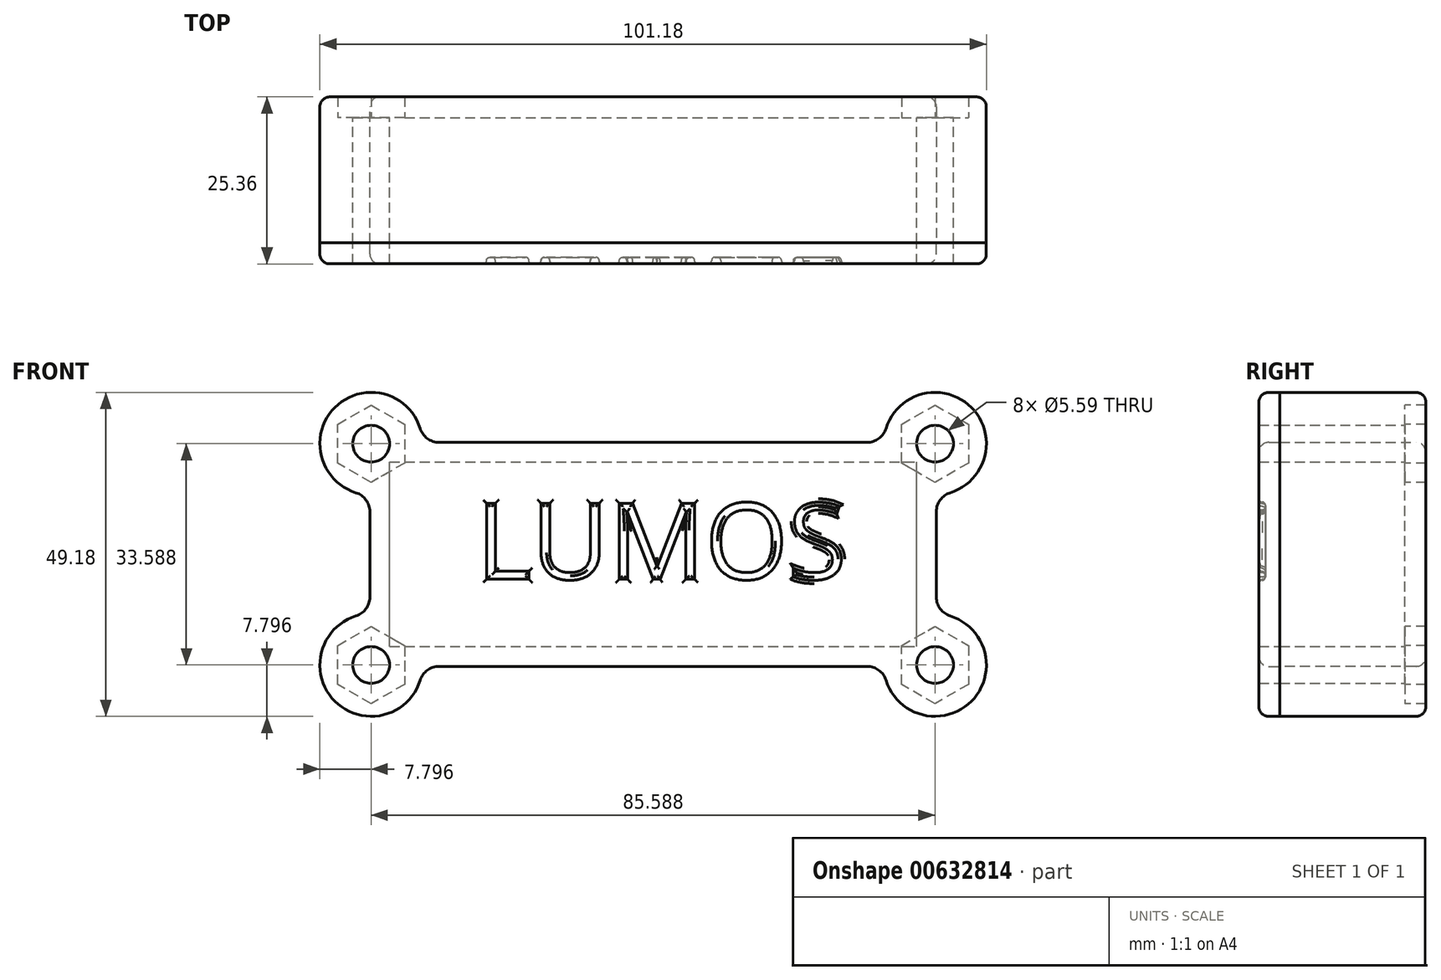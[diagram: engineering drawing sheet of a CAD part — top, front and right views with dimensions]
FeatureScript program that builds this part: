
annotation { "Feature Type Name" : "Feature", "Feature Type Description" : "" }
export const myFeature = defineFeature(function(context is Context, id is Id, definition is map)
    precondition{}
    {
        {
            var Q0;
            Q0=qCreatedBy(makeId("Front.planeOp"),FACE);
            var sketch = newSketch(context, id + "F0", { "sketchPlane" : qUnion([Q0])});
            skLineSegment(sketch, "E0.bottom", {"start": v(0, 0) * mm, "end": v(80, 0) * mm});
            skLineSegment(sketch, "E0.top", {"start": v(0, 28) * mm, "end": v(80, 28) * mm});
            skLineSegment(sketch, "E0.left", {"start": v(0, 0) * mm, "end": v(0, 28) * mm});
            skLineSegment(sketch, "E0.right", {"start": v(80, 0) * mm, "end": v(80, 28) * mm});
            skCircle(sketch, "E1", {"center": v(82.8, 30.8) * mm, "radius": 2.8 * mm});
            skCircle(sketch, "E2", {"center": v(82.8, -2.8) * mm, "radius": 2.8 * mm});
            skCircle(sketch, "E3", {"center": v(-2.8, -2.8) * mm, "radius": 2.8 * mm});
            skCircle(sketch, "E4", {"center": v(-2.8, 30.8) * mm, "radius": 2.8 * mm});
            skArc(sketch, "E5", {"start": v(5, 31) * mm, "mid": v(-8.3, 36.3) * mm, "end": v(-3, 23) * mm});
            skArc(sketch, "E6", {"start": v(83, 23) * mm, "mid": v(88.3, 36.3) * mm, "end": v(75, 31) * mm});
            skArc(sketch, "E7", {"start": v(75, -3) * mm, "mid": v(88.3, -8.3) * mm, "end": v(83, 5) * mm});
            skLineSegment(sketch, "E8.0", {"start": v(5, 31) * mm, "end": v(75, 31) * mm});
            skLineSegment(sketch, "E8.1", {"start": v(-3, 5) * mm, "end": v(-3, 23) * mm});
            skLineSegment(sketch, "E8.2", {"start": v(5, -3) * mm, "end": v(75, -3) * mm});
            skLineSegment(sketch, "E8.3", {"start": v(83, 5) * mm, "end": v(83, 23) * mm});
            skArc(sketch, "E9.trimOffspring", {"start": v(-3, 5) * mm, "mid": v(-8.3, -8.3) * mm, "end": v(5, -3) * mm});
            skSolve(sketch);
        }
        {
            var Q0;
            Q0=makeQuery(id+"F0.imprint","IMPRINT",FACE,{"disambiguationData":[TD([[makeQuery(id+"F0.imprint","IMPRINT",EDGE,{"derivedFrom":sQuery(id+"F0.wireOp",EDGE,"E0.bottom")}),-1.0]])]});
            extrude(context, id + "F1", {"entities" : qUnion([Q0]), "depth" : 19 * mm, "offsetDistance" : 25 * mm});
        }
        {
            var Q0;
            Q0=qCreatedBy(makeId("Front.planeOp"),FACE);
            var sketch = newSketch(context, id + "F2", { "sketchPlane" : qUnion([Q0])});
            skLineSegment(sketch, "E10.0", {"start": v(5, -3) * mm, "end": v(75, -3) * mm});
            skArc(sketch, "E11.0", {"start": v(-3, 5) * mm, "mid": v(-8.3, -8.3) * mm, "end": v(5, -3) * mm});
            skArc(sketch, "E12.0", {"start": v(75, -3) * mm, "mid": v(88.3, -8.3) * mm, "end": v(83, 5) * mm});
            skLineSegment(sketch, "E13.0", {"start": v(83, 5) * mm, "end": v(83, 23) * mm});
            skArc(sketch, "E14.0", {"start": v(83, 23) * mm, "mid": v(88.3, 36.3) * mm, "end": v(75, 31) * mm});
            skLineSegment(sketch, "E15.0", {"start": v(5, 31) * mm, "end": v(75, 31) * mm});
            skArc(sketch, "E16.0", {"start": v(5, 31) * mm, "mid": v(-8.3, 36.3) * mm, "end": v(-3, 23) * mm});
            skLineSegment(sketch, "E17.0", {"start": v(-3, 5) * mm, "end": v(-3, 23) * mm});
            skCircle(sketch, "E18.0", {"center": v(-2.8, -2.8) * mm, "radius": 2.8 * mm});
            skCircle(sketch, "E19.0", {"center": v(-2.8, 30.8) * mm, "radius": 2.8 * mm});
            skCircle(sketch, "E20.0", {"center": v(82.8, -2.8) * mm, "radius": 2.8 * mm});
            skCircle(sketch, "E21.0", {"center": v(82.8, 30.8) * mm, "radius": 2.8 * mm});
            skSolve(sketch);
        }
        {
            var Q0;
            Q0 = qSketchRegion(id + "F2", true);
            extrude(context, id + "F3", {"entities" : qUnion([Q0]), "operationType" : NewBodyOperationType.ADD, "oppositeDirection" : true, "depth" : 3.17 * mm, "offsetDistance" : 25 * mm});
        }
        {
            var Q0;
            Q0=makeQuery(id+"F3.boolean.opBoolean","MERGE",EDGE,{"derivedFrom":[makeQuery(id+"F1.opExtrude","SWEPT_EDGE",EDGE,{"disambiguationData":[OSD([sQuery(id+"F0.wireOp",EDGE,"E8.2"),sQuery(id+"F0.wireOp",EDGE,"E9.trimOffspring")])]}),makeQuery(id+"F3.opExtrude","SWEPT_EDGE",EDGE,{"disambiguationData":[OSD([sQuery(id+"F2.wireOp",EDGE,"E10.0"),sQuery(id+"F2.wireOp",EDGE,"E11.0")])]})]});
            var Q1;
            Q1=makeQuery(id+"F3.boolean.opBoolean","MERGE",EDGE,{"derivedFrom":[makeQuery(id+"F1.opExtrude","SWEPT_EDGE",EDGE,{"disambiguationData":[OSD([sQuery(id+"F0.wireOp",EDGE,"E6"),sQuery(id+"F0.wireOp",EDGE,"E8.3")])]}),makeQuery(id+"F3.opExtrude","SWEPT_EDGE",EDGE,{"disambiguationData":[OSD([sQuery(id+"F2.wireOp",EDGE,"E13.0"),sQuery(id+"F2.wireOp",EDGE,"E14.0")])]})]});
            var Q2;
            Q2=makeQuery(id+"F3.boolean.opBoolean","MERGE",EDGE,{"derivedFrom":[makeQuery(id+"F1.opExtrude","SWEPT_EDGE",EDGE,{"disambiguationData":[OSD([sQuery(id+"F0.wireOp",EDGE,"E7"),sQuery(id+"F0.wireOp",EDGE,"E8.2")])]}),makeQuery(id+"F3.opExtrude","SWEPT_EDGE",EDGE,{"disambiguationData":[OSD([sQuery(id+"F2.wireOp",EDGE,"E10.0"),sQuery(id+"F2.wireOp",EDGE,"E12.0")])]})]});
            var Q3;
            Q3=makeQuery(id+"F3.boolean.opBoolean","MERGE",EDGE,{"derivedFrom":[makeQuery(id+"F1.opExtrude","SWEPT_EDGE",EDGE,{"disambiguationData":[OSD([sQuery(id+"F0.wireOp",EDGE,"E7"),sQuery(id+"F0.wireOp",EDGE,"E8.3")])]}),makeQuery(id+"F3.opExtrude","SWEPT_EDGE",EDGE,{"disambiguationData":[OSD([sQuery(id+"F2.wireOp",EDGE,"E12.0"),sQuery(id+"F2.wireOp",EDGE,"E13.0")])]})]});
            var Q4;
            Q4=makeQuery(id+"F3.boolean.opBoolean","MERGE",EDGE,{"derivedFrom":[makeQuery(id+"F1.opExtrude","SWEPT_EDGE",EDGE,{"disambiguationData":[OSD([sQuery(id+"F0.wireOp",EDGE,"E6"),sQuery(id+"F0.wireOp",EDGE,"E8.0")])]}),makeQuery(id+"F3.opExtrude","SWEPT_EDGE",EDGE,{"disambiguationData":[OSD([sQuery(id+"F2.wireOp",EDGE,"E14.0"),sQuery(id+"F2.wireOp",EDGE,"E15.0")])]})]});
            var Q5;
            Q5=makeQuery(id+"F3.boolean.opBoolean","MERGE",EDGE,{"derivedFrom":[makeQuery(id+"F1.opExtrude","SWEPT_EDGE",EDGE,{"disambiguationData":[OSD([sQuery(id+"F0.wireOp",EDGE,"E8.1"),sQuery(id+"F0.wireOp",EDGE,"E9.trimOffspring")])]}),makeQuery(id+"F3.opExtrude","SWEPT_EDGE",EDGE,{"disambiguationData":[OSD([sQuery(id+"F2.wireOp",EDGE,"E11.0"),sQuery(id+"F2.wireOp",EDGE,"E17.0")])]})]});
            var Q6;
            Q6=makeQuery(id+"F3.boolean.opBoolean","MERGE",EDGE,{"derivedFrom":[makeQuery(id+"F1.opExtrude","SWEPT_EDGE",EDGE,{"disambiguationData":[OSD([sQuery(id+"F0.wireOp",EDGE,"E5"),sQuery(id+"F0.wireOp",EDGE,"E8.1")])]}),makeQuery(id+"F3.opExtrude","SWEPT_EDGE",EDGE,{"disambiguationData":[OSD([sQuery(id+"F2.wireOp",EDGE,"E16.0"),sQuery(id+"F2.wireOp",EDGE,"E17.0")])]})]});
            var Q7;
            Q7=makeQuery(id+"F3.boolean.opBoolean","MERGE",EDGE,{"derivedFrom":[makeQuery(id+"F1.opExtrude","SWEPT_EDGE",EDGE,{"disambiguationData":[OSD([sQuery(id+"F0.wireOp",EDGE,"E5"),sQuery(id+"F0.wireOp",EDGE,"E8.0")])]}),makeQuery(id+"F3.opExtrude","SWEPT_EDGE",EDGE,{"disambiguationData":[OSD([sQuery(id+"F2.wireOp",EDGE,"E15.0"),sQuery(id+"F2.wireOp",EDGE,"E16.0")])]})]});
            fillet(context, id + "F4", {"entities" : qUnion([Q0, Q1, Q2, Q3, Q4, Q5, Q6, Q7]), "radius" : 3 * mm, "tangentPropagation" : true, "allowEdgeOverflow" : false});
        }
        {
            var Q0;
            Q0=makeQuery(id+"F3.opExtrude","CAP_EDGE",EDGE,{"disambiguationData":[OSD([sQuery(id+"F2.wireOp",EDGE,"E15.0")])],"isStart":false});
            fillet(context, id + "F5", {"entities" : qUnion([Q0]), "radius" : 1.5 * mm, "tangentPropagation" : true, "allowEdgeOverflow" : false});
        }
        {
            var Q0;
            Q0=qCreatedBy(makeId("Front.planeOp"),FACE);
            var sketch = newSketch(context, id + "F6", { "sketchPlane" : qUnion([Q0])});
            skCircle(sketch, "E22.cCircle", {"center": v(-2.8, -2.8) * mm, "radius": 5.08 * mm, "construction": true});
            skLineSegment(sketch, "E22.0", {"start": v(2.29, 0.14) * mm, "end": v(2.29, -5.73) * mm});
            skLineSegment(sketch, "E22.1", {"start": v(2.29, -5.73) * mm, "end": v(-2.8, -8.66) * mm});
            skLineSegment(sketch, "E22.2", {"start": v(-2.8, -8.66) * mm, "end": v(-7.87, -5.73) * mm});
            skLineSegment(sketch, "E22.3", {"start": v(-7.87, -5.73) * mm, "end": v(-7.87, 0.14) * mm});
            skLineSegment(sketch, "E22.4", {"start": v(-7.87, 0.14) * mm, "end": v(-2.8, 3.07) * mm});
            skLineSegment(sketch, "E22.5", {"start": v(-2.8, 3.07) * mm, "end": v(2.29, 0.14) * mm});
            skPoint(sketch, "E22.0.midPoint", {"position": v(2.29, -2.8) * mm});
            skCircle(sketch, "E23.cCircle", {"center": v(-2.8, 30.8) * mm, "radius": 5.08 * mm, "construction": true});
            skLineSegment(sketch, "E23.0", {"start": v(2.29, 33.73) * mm, "end": v(2.29, 27.86) * mm});
            skLineSegment(sketch, "E23.1", {"start": v(2.29, 27.86) * mm, "end": v(-2.8, 24.93) * mm});
            skLineSegment(sketch, "E23.2", {"start": v(-2.8, 24.93) * mm, "end": v(-7.87, 27.86) * mm});
            skLineSegment(sketch, "E23.3", {"start": v(-7.87, 27.86) * mm, "end": v(-7.87, 33.73) * mm});
            skLineSegment(sketch, "E23.4", {"start": v(-7.87, 33.73) * mm, "end": v(-2.8, 36.66) * mm});
            skLineSegment(sketch, "E23.5", {"start": v(-2.8, 36.66) * mm, "end": v(2.29, 33.73) * mm});
            skPoint(sketch, "E23.0.midPoint", {"position": v(2.29, 30.8) * mm});
            skCircle(sketch, "E24.cCircle", {"center": v(82.8, 30.8) * mm, "radius": 5.08 * mm, "construction": true});
            skLineSegment(sketch, "E24.0", {"start": v(87.87, 33.73) * mm, "end": v(87.87, 27.86) * mm});
            skLineSegment(sketch, "E24.1", {"start": v(87.87, 27.86) * mm, "end": v(82.8, 24.93) * mm});
            skLineSegment(sketch, "E24.2", {"start": v(82.8, 24.93) * mm, "end": v(77.71, 27.86) * mm});
            skLineSegment(sketch, "E24.3", {"start": v(77.71, 27.86) * mm, "end": v(77.71, 33.73) * mm});
            skLineSegment(sketch, "E24.4", {"start": v(77.71, 33.73) * mm, "end": v(82.8, 36.66) * mm});
            skLineSegment(sketch, "E24.5", {"start": v(82.8, 36.66) * mm, "end": v(87.87, 33.73) * mm});
            skPoint(sketch, "E24.0.midPoint", {"position": v(87.87, 30.8) * mm});
            skCircle(sketch, "E25.cCircle", {"center": v(82.8, -2.8) * mm, "radius": 5.08 * mm, "construction": true});
            skLineSegment(sketch, "E25.0", {"start": v(77.71, -5.73) * mm, "end": v(77.71, 0.14) * mm});
            skLineSegment(sketch, "E25.1", {"start": v(77.71, 0.14) * mm, "end": v(82.8, 3.07) * mm});
            skLineSegment(sketch, "E25.2", {"start": v(82.8, 3.07) * mm, "end": v(87.87, 0.14) * mm});
            skLineSegment(sketch, "E25.3", {"start": v(87.87, 0.14) * mm, "end": v(87.87, -5.73) * mm});
            skLineSegment(sketch, "E25.4", {"start": v(87.87, -5.73) * mm, "end": v(82.8, -8.66) * mm});
            skLineSegment(sketch, "E25.5", {"start": v(82.8, -8.66) * mm, "end": v(77.71, -5.73) * mm});
            skPoint(sketch, "E25.0.midPoint", {"position": v(77.71, -2.8) * mm});
            skSolve(sketch);
        }
        {
            var Q0;
            Q0 = qSketchRegion(id + "F6", true);
            extrude(context, id + "F7", {"entities" : qUnion([Q0]), "operationType" : NewBodyOperationType.REMOVE, "oppositeDirection" : true, "depth" : 25 * mm, "offsetDistance" : 25 * mm});
        }
        {
            var Q0;
            Q0=makeQuery(id+"F1.opExtrude","CAP_FACE",FACE,{"disambiguationData":[OSD([sQuery(id+"F0.wireOp",EDGE,"E0.bottom"),sQuery(id+"F0.wireOp",EDGE,"E0.top"),sQuery(id+"F0.wireOp",EDGE,"E0.left"),sQuery(id+"F0.wireOp",EDGE,"E0.right"),sQuery(id+"F0.wireOp",EDGE,"E1"),sQuery(id+"F0.wireOp",EDGE,"E2"),sQuery(id+"F0.wireOp",EDGE,"E3"),sQuery(id+"F0.wireOp",EDGE,"E4"),sQuery(id+"F0.wireOp",EDGE,"E5"),sQuery(id+"F0.wireOp",EDGE,"E6"),sQuery(id+"F0.wireOp",EDGE,"E7"),sQuery(id+"F0.wireOp",EDGE,"E8.0"),sQuery(id+"F0.wireOp",EDGE,"E8.1"),sQuery(id+"F0.wireOp",EDGE,"E8.2"),sQuery(id+"F0.wireOp",EDGE,"E8.3"),sQuery(id+"F0.wireOp",EDGE,"E9.trimOffspring")])],"isStart":false});
            var sketch = newSketch(context, id + "F8", { "sketchPlane" : qUnion([Q0])});
            skArc(sketch, "E26.0", {"start": v(4.65, 33.1) * mm, "mid": v(-8.3, 36.3) * mm, "end": v(-5.1, 23.35) * mm});
            skArc(sketch, "E26.1", {"start": v(7.51, 31) * mm, "mid": v(5.73, 31.58) * mm, "end": v(4.65, 33.1) * mm});
            skLineSegment(sketch, "E26.2", {"start": v(7.51, 31) * mm, "end": v(72.49, 31) * mm});
            skArc(sketch, "E26.3", {"start": v(75.35, 33.1) * mm, "mid": v(74.27, 31.58) * mm, "end": v(72.49, 31) * mm});
            skArc(sketch, "E26.4", {"start": v(85.1, 23.35) * mm, "mid": v(88.3, 36.3) * mm, "end": v(75.35, 33.1) * mm});
            skLineSegment(sketch, "E26.5", {"start": v(83, 7.51) * mm, "end": v(83, 20.49) * mm});
            skArc(sketch, "E26.6", {"start": v(83, 20.49) * mm, "mid": v(83.58, 22.27) * mm, "end": v(85.1, 23.35) * mm});
            skArc(sketch, "E26.7", {"start": v(85.1, 4.65) * mm, "mid": v(83.58, 5.73) * mm, "end": v(83, 7.51) * mm});
            skArc(sketch, "E26.8", {"start": v(75.35, -5.1) * mm, "mid": v(88.3, -8.3) * mm, "end": v(85.1, 4.65) * mm});
            skLineSegment(sketch, "E26.9", {"start": v(7.51, -3) * mm, "end": v(72.49, -3) * mm});
            skArc(sketch, "E26.10", {"start": v(72.49, -3) * mm, "mid": v(74.27, -3.58) * mm, "end": v(75.35, -5.1) * mm});
            skArc(sketch, "E26.11", {"start": v(4.65, -5.1) * mm, "mid": v(5.73, -3.58) * mm, "end": v(7.51, -3) * mm});
            skArc(sketch, "E26.12", {"start": v(-5.1, 4.65) * mm, "mid": v(-8.3, -8.3) * mm, "end": v(4.65, -5.1) * mm});
            skArc(sketch, "E26.13", {"start": v(-3, 7.51) * mm, "mid": v(-3.58, 5.73) * mm, "end": v(-5.1, 4.65) * mm});
            skLineSegment(sketch, "E26.14", {"start": v(-3, 7.51) * mm, "end": v(-3, 20.49) * mm});
            skArc(sketch, "E26.15", {"start": v(-5.1, 23.35) * mm, "mid": v(-3.58, 22.27) * mm, "end": v(-3, 20.49) * mm});
            skCircle(sketch, "E26.16", {"center": v(-2.8, -2.8) * mm, "radius": 2.8 * mm});
            skCircle(sketch, "E26.17", {"center": v(-2.8, 30.8) * mm, "radius": 2.8 * mm});
            skCircle(sketch, "E26.18", {"center": v(82.8, 30.8) * mm, "radius": 2.8 * mm});
            skCircle(sketch, "E26.19", {"center": v(82.8, -2.8) * mm, "radius": 2.8 * mm});
            skPoint(sketch, "E26.20", {"position": v(74.27, 31.58) * mm});
            skSolve(sketch);
        }
        {
            var Q0;
            Q0 = qSketchRegion(id + "F8", true);
            extrude(context, id + "F9", {"entities" : qUnion([Q0]), "depth" : 3.17 * mm, "offsetDistance" : 25 * mm});
        }
        {
            var Q0;
            Q0=makeQuery(id+"F9.opExtrude","CAP_EDGE",EDGE,{"disambiguationData":[OSD([sQuery(id+"F8.wireOp",EDGE,"E26.4")])],"isStart":false});
            fillet(context, id + "F10", {"entities" : qUnion([Q0]), "radius" : 1.5 * mm, "tangentPropagation" : true, "allowEdgeOverflow" : false});
        }
        {
            var Q0;
            Q0=makeQuery(id+"F9.opExtrude","CAP_FACE",FACE,{"disambiguationData":[OSD([sQuery(id+"F8.wireOp",EDGE,"E26.0"),sQuery(id+"F8.wireOp",EDGE,"E26.1"),sQuery(id+"F8.wireOp",EDGE,"E26.2"),sQuery(id+"F8.wireOp",EDGE,"E26.3"),sQuery(id+"F8.wireOp",EDGE,"E26.4"),sQuery(id+"F8.wireOp",EDGE,"E26.5"),sQuery(id+"F8.wireOp",EDGE,"E26.6"),sQuery(id+"F8.wireOp",EDGE,"E26.7"),sQuery(id+"F8.wireOp",EDGE,"E26.8"),sQuery(id+"F8.wireOp",EDGE,"E26.9"),sQuery(id+"F8.wireOp",EDGE,"E26.10"),sQuery(id+"F8.wireOp",EDGE,"E26.11"),sQuery(id+"F8.wireOp",EDGE,"E26.12"),sQuery(id+"F8.wireOp",EDGE,"E26.13"),sQuery(id+"F8.wireOp",EDGE,"E26.14"),sQuery(id+"F8.wireOp",EDGE,"E26.15"),sQuery(id+"F8.wireOp",EDGE,"E26.16"),sQuery(id+"F8.wireOp",EDGE,"E26.17"),sQuery(id+"F8.wireOp",EDGE,"E26.18"),sQuery(id+"F8.wireOp",EDGE,"E26.19")])],"isStart":false});
            var sketch = newSketch(context, id + "F11", { "sketchPlane" : qUnion([Q0])});
            skText(sketch, "E27", { "text": "LUMOS\n", "fontName": "OpenSans-Regular.ttf"});
            const initialGuessF11  = {"E27": [0.01313, 0.01022, 1, 0, 0.01164]};
            skSetInitialGuess(sketch, initialGuessF11);
            skSolve(sketch);
        }
        {
            var Q0;
            Q0 = qSketchRegion(id + "F11", true);
            extrude(context, id + "F12", {"entities" : qUnion([Q0]), "operationType" : NewBodyOperationType.REMOVE, "oppositeDirection" : true, "depth" : 1 * mm, "offsetDistance" : 25 * mm});
        }
        {
            var Q0;
            Q0=makeQuery(id+"F12.boolean.opBoolean","COPY",FACE,{"derivedFrom":makeQuery(id+"F12.opExtrude","CAP_FACE",FACE,{"disambiguationData":[OSD([sQuery(id+"F11.wireOp",EDGE,"E27.sketch_text.stroke-0"),sQuery(id+"F11.wireOp",EDGE,"E27.sketch_text.stroke-1"),sQuery(id+"F11.wireOp",EDGE,"E27.sketch_text.stroke-2"),sQuery(id+"F11.wireOp",EDGE,"E27.sketch_text.stroke-3"),sQuery(id+"F11.wireOp",EDGE,"E27.sketch_text.stroke-4"),sQuery(id+"F11.wireOp",EDGE,"E27.sketch_text.stroke-5")])],"isStart":false})});
            var Q1;
            Q1=makeQuery(id+"F12.boolean.opBoolean","COPY",FACE,{"derivedFrom":makeQuery(id+"F12.opExtrude","CAP_FACE",FACE,{"disambiguationData":[OSD([sQuery(id+"F11.wireOp",EDGE,"E27.sketch_text.stroke-6"),sQuery(id+"F11.wireOp",EDGE,"E27.sketch_text.stroke-7"),sQuery(id+"F11.wireOp",EDGE,"E27.sketch_text.stroke-8"),sQuery(id+"F11.wireOp",EDGE,"E27.sketch_text.stroke-9"),sQuery(id+"F11.wireOp",EDGE,"E27.sketch_text.stroke-10"),sQuery(id+"F11.wireOp",EDGE,"E27.sketch_text.stroke-11"),sQuery(id+"F11.wireOp",EDGE,"E27.sketch_text.stroke-12"),sQuery(id+"F11.wireOp",EDGE,"E27.sketch_text.stroke-13"),sQuery(id+"F11.wireOp",EDGE,"E27.sketch_text.stroke-14"),sQuery(id+"F11.wireOp",EDGE,"E27.sketch_text.stroke-15"),sQuery(id+"F11.wireOp",EDGE,"E27.sketch_text.stroke-16"),sQuery(id+"F11.wireOp",EDGE,"E27.sketch_text.stroke-17"),sQuery(id+"F11.wireOp",EDGE,"E27.sketch_text.stroke-18"),sQuery(id+"F11.wireOp",EDGE,"E27.sketch_text.stroke-19")])],"isStart":false})});
            var Q2;
            Q2=makeQuery(id+"F12.boolean.opBoolean","COPY",FACE,{"derivedFrom":makeQuery(id+"F12.opExtrude","CAP_FACE",FACE,{"disambiguationData":[OSD([sQuery(id+"F11.wireOp",EDGE,"E27.sketch_text.stroke-20"),sQuery(id+"F11.wireOp",EDGE,"E27.sketch_text.stroke-21"),sQuery(id+"F11.wireOp",EDGE,"E27.sketch_text.stroke-22"),sQuery(id+"F11.wireOp",EDGE,"E27.sketch_text.stroke-23"),sQuery(id+"F11.wireOp",EDGE,"E27.sketch_text.stroke-24"),sQuery(id+"F11.wireOp",EDGE,"E27.sketch_text.stroke-25"),sQuery(id+"F11.wireOp",EDGE,"E27.sketch_text.stroke-26"),sQuery(id+"F11.wireOp",EDGE,"E27.sketch_text.stroke-27"),sQuery(id+"F11.wireOp",EDGE,"E27.sketch_text.stroke-28"),sQuery(id+"F11.wireOp",EDGE,"E27.sketch_text.stroke-29"),sQuery(id+"F11.wireOp",EDGE,"E27.sketch_text.stroke-30"),sQuery(id+"F11.wireOp",EDGE,"E27.sketch_text.stroke-31"),sQuery(id+"F11.wireOp",EDGE,"E27.sketch_text.stroke-32"),sQuery(id+"F11.wireOp",EDGE,"E27.sketch_text.stroke-33"),sQuery(id+"F11.wireOp",EDGE,"E27.sketch_text.stroke-34"),sQuery(id+"F11.wireOp",EDGE,"E27.sketch_text.stroke-35"),sQuery(id+"F11.wireOp",EDGE,"E27.sketch_text.stroke-36"),sQuery(id+"F11.wireOp",EDGE,"E27.sketch_text.stroke-37")])],"isStart":false})});
            var Q3;
            Q3=makeQuery(id+"F12.boolean.opBoolean","COPY",FACE,{"derivedFrom":makeQuery(id+"F12.opExtrude","CAP_FACE",FACE,{"disambiguationData":[OSD([sQuery(id+"F11.wireOp",EDGE,"E27.sketch_text.stroke-38"),sQuery(id+"F11.wireOp",EDGE,"E27.sketch_text.stroke-39"),sQuery(id+"F11.wireOp",EDGE,"E27.sketch_text.stroke-40"),sQuery(id+"F11.wireOp",EDGE,"E27.sketch_text.stroke-41"),sQuery(id+"F11.wireOp",EDGE,"E27.sketch_text.stroke-42"),sQuery(id+"F11.wireOp",EDGE,"E27.sketch_text.stroke-43"),sQuery(id+"F11.wireOp",EDGE,"E27.sketch_text.stroke-44"),sQuery(id+"F11.wireOp",EDGE,"E27.sketch_text.stroke-45"),sQuery(id+"F11.wireOp",EDGE,"E27.sketch_text.stroke-46"),sQuery(id+"F11.wireOp",EDGE,"E27.sketch_text.stroke-47"),sQuery(id+"F11.wireOp",EDGE,"E27.sketch_text.stroke-48"),sQuery(id+"F11.wireOp",EDGE,"E27.sketch_text.stroke-49"),sQuery(id+"F11.wireOp",EDGE,"E27.sketch_text.stroke-50"),sQuery(id+"F11.wireOp",EDGE,"E27.sketch_text.stroke-51"),sQuery(id+"F11.wireOp",EDGE,"E27.sketch_text.stroke-52"),sQuery(id+"F11.wireOp",EDGE,"E27.sketch_text.stroke-53")])],"isStart":false})});
            var Q4;
            Q4=makeQuery(id+"F12.boolean.opBoolean","COPY",FACE,{"derivedFrom":makeQuery(id+"F12.opExtrude","CAP_FACE",FACE,{"disambiguationData":[OSD([sQuery(id+"F11.wireOp",EDGE,"E27.sketch_text.stroke-54"),sQuery(id+"F11.wireOp",EDGE,"E27.sketch_text.stroke-55"),sQuery(id+"F11.wireOp",EDGE,"E27.sketch_text.stroke-56"),sQuery(id+"F11.wireOp",EDGE,"E27.sketch_text.stroke-57"),sQuery(id+"F11.wireOp",EDGE,"E27.sketch_text.stroke-58"),sQuery(id+"F11.wireOp",EDGE,"E27.sketch_text.stroke-59"),sQuery(id+"F11.wireOp",EDGE,"E27.sketch_text.stroke-60"),sQuery(id+"F11.wireOp",EDGE,"E27.sketch_text.stroke-61"),sQuery(id+"F11.wireOp",EDGE,"E27.sketch_text.stroke-62"),sQuery(id+"F11.wireOp",EDGE,"E27.sketch_text.stroke-63"),sQuery(id+"F11.wireOp",EDGE,"E27.sketch_text.stroke-64"),sQuery(id+"F11.wireOp",EDGE,"E27.sketch_text.stroke-65"),sQuery(id+"F11.wireOp",EDGE,"E27.sketch_text.stroke-66"),sQuery(id+"F11.wireOp",EDGE,"E27.sketch_text.stroke-67"),sQuery(id+"F11.wireOp",EDGE,"E27.sketch_text.stroke-68"),sQuery(id+"F11.wireOp",EDGE,"E27.sketch_text.stroke-69"),sQuery(id+"F11.wireOp",EDGE,"E27.sketch_text.stroke-70"),sQuery(id+"F11.wireOp",EDGE,"E27.sketch_text.stroke-71"),sQuery(id+"F11.wireOp",EDGE,"E27.sketch_text.stroke-72"),sQuery(id+"F11.wireOp",EDGE,"E27.sketch_text.stroke-73"),sQuery(id+"F11.wireOp",EDGE,"E27.sketch_text.stroke-74"),sQuery(id+"F11.wireOp",EDGE,"E27.sketch_text.stroke-75"),sQuery(id+"F11.wireOp",EDGE,"E27.sketch_text.stroke-76"),sQuery(id+"F11.wireOp",EDGE,"E27.sketch_text.stroke-77"),sQuery(id+"F11.wireOp",EDGE,"E27.sketch_text.stroke-78")])],"isStart":false})});
            fillet(context, id + "F13", {"entities" : qUnion([Q0, Q1, Q2, Q3, Q4]), "radius" : .5 * mm, "tangentPropagation" : true, "allowEdgeOverflow" : false});
        }
        {
            var Q0;
            Q0=makeQuery(id+"F12.boolean.opBoolean","COPY",EDGE,{"derivedFrom":makeQuery(id+"F12.opExtrude","CAP_EDGE",EDGE,{"disambiguationData":[OSD([sQuery(id+"F11.wireOp",EDGE,"E27.sketch_text.stroke-0")])],"isStart":true})});
            var Q1;
            Q1=makeQuery(id+"F12.boolean.opBoolean","COPY",EDGE,{"derivedFrom":makeQuery(id+"F12.opExtrude","CAP_EDGE",EDGE,{"disambiguationData":[OSD([sQuery(id+"F11.wireOp",EDGE,"E27.sketch_text.stroke-5")])],"isStart":true})});
            var Q2;
            Q2=makeQuery(id+"F12.boolean.opBoolean","COPY",EDGE,{"derivedFrom":makeQuery(id+"F12.opExtrude","CAP_EDGE",EDGE,{"disambiguationData":[OSD([sQuery(id+"F11.wireOp",EDGE,"E27.sketch_text.stroke-3")])],"isStart":true})});
            var Q3;
            Q3=makeQuery(id+"F12.boolean.opBoolean","COPY",EDGE,{"derivedFrom":makeQuery(id+"F12.opExtrude","CAP_EDGE",EDGE,{"disambiguationData":[OSD([sQuery(id+"F11.wireOp",EDGE,"E27.sketch_text.stroke-4")])],"isStart":true})});
            var Q4;
            Q4=makeQuery(id+"F12.boolean.opBoolean","COPY",EDGE,{"derivedFrom":makeQuery(id+"F12.opExtrude","CAP_EDGE",EDGE,{"disambiguationData":[OSD([sQuery(id+"F11.wireOp",EDGE,"E27.sketch_text.stroke-2")])],"isStart":true})});
            var Q5;
            Q5=makeQuery(id+"F12.boolean.opBoolean","COPY",EDGE,{"derivedFrom":makeQuery(id+"F12.opExtrude","CAP_EDGE",EDGE,{"disambiguationData":[OSD([sQuery(id+"F11.wireOp",EDGE,"E27.sketch_text.stroke-1")])],"isStart":true})});
            var Q6;
            Q6=makeQuery(id+"F12.boolean.opBoolean","COPY",EDGE,{"derivedFrom":makeQuery(id+"F12.opExtrude","CAP_EDGE",EDGE,{"disambiguationData":[OSD([sQuery(id+"F11.wireOp",EDGE,"E27.sketch_text.stroke-12")])],"isStart":true})});
            var Q7;
            Q7=makeQuery(id+"F12.boolean.opBoolean","COPY",EDGE,{"derivedFrom":makeQuery(id+"F12.opExtrude","CAP_EDGE",EDGE,{"disambiguationData":[OSD([sQuery(id+"F11.wireOp",EDGE,"E27.sketch_text.stroke-11")])],"isStart":true})});
            var Q8;
            Q8=makeQuery(id+"F12.boolean.opBoolean","COPY",EDGE,{"derivedFrom":makeQuery(id+"F12.opExtrude","CAP_EDGE",EDGE,{"disambiguationData":[OSD([sQuery(id+"F11.wireOp",EDGE,"E27.sketch_text.stroke-16")])],"isStart":true})});
            var Q9;
            Q9=makeQuery(id+"F12.boolean.opBoolean","COPY",EDGE,{"derivedFrom":makeQuery(id+"F12.opExtrude","CAP_EDGE",EDGE,{"disambiguationData":[OSD([sQuery(id+"F11.wireOp",EDGE,"E27.sketch_text.stroke-19")])],"isStart":true})});
            var Q10;
            Q10=makeQuery(id+"F12.boolean.opBoolean","COPY",EDGE,{"derivedFrom":makeQuery(id+"F12.opExtrude","CAP_EDGE",EDGE,{"disambiguationData":[OSD([sQuery(id+"F11.wireOp",EDGE,"E27.sketch_text.stroke-25")])],"isStart":true})});
            var Q11;
            Q11=makeQuery(id+"F12.boolean.opBoolean","COPY",EDGE,{"derivedFrom":makeQuery(id+"F12.opExtrude","CAP_EDGE",EDGE,{"disambiguationData":[OSD([sQuery(id+"F11.wireOp",EDGE,"E27.sketch_text.stroke-26")])],"isStart":true})});
            var Q12;
            Q12=makeQuery(id+"F12.boolean.opBoolean","COPY",EDGE,{"derivedFrom":makeQuery(id+"F12.opExtrude","CAP_EDGE",EDGE,{"disambiguationData":[OSD([sQuery(id+"F11.wireOp",EDGE,"E27.sketch_text.stroke-23")])],"isStart":true})});
            var Q13;
            Q13=makeQuery(id+"F12.boolean.opBoolean","COPY",EDGE,{"derivedFrom":makeQuery(id+"F12.opExtrude","CAP_EDGE",EDGE,{"disambiguationData":[OSD([sQuery(id+"F11.wireOp",EDGE,"E27.sketch_text.stroke-24")])],"isStart":true})});
            var Q14;
            Q14=makeQuery(id+"F12.boolean.opBoolean","COPY",EDGE,{"derivedFrom":makeQuery(id+"F12.opExtrude","CAP_EDGE",EDGE,{"disambiguationData":[OSD([sQuery(id+"F11.wireOp",EDGE,"E27.sketch_text.stroke-20")])],"isStart":true})});
            var Q15;
            Q15=makeQuery(id+"F12.boolean.opBoolean","COPY",EDGE,{"derivedFrom":makeQuery(id+"F12.opExtrude","CAP_EDGE",EDGE,{"disambiguationData":[OSD([sQuery(id+"F11.wireOp",EDGE,"E27.sketch_text.stroke-27")])],"isStart":true})});
            var Q16;
            Q16=makeQuery(id+"F12.boolean.opBoolean","COPY",EDGE,{"derivedFrom":makeQuery(id+"F12.opExtrude","CAP_EDGE",EDGE,{"disambiguationData":[OSD([sQuery(id+"F11.wireOp",EDGE,"E27.sketch_text.stroke-29")])],"isStart":true})});
            var Q17;
            Q17=makeQuery(id+"F12.boolean.opBoolean","COPY",EDGE,{"derivedFrom":makeQuery(id+"F12.opExtrude","CAP_EDGE",EDGE,{"disambiguationData":[OSD([sQuery(id+"F11.wireOp",EDGE,"E27.sketch_text.stroke-37")])],"isStart":true})});
            var Q18;
            Q18=makeQuery(id+"F12.boolean.opBoolean","COPY",EDGE,{"derivedFrom":makeQuery(id+"F12.opExtrude","CAP_EDGE",EDGE,{"disambiguationData":[OSD([sQuery(id+"F11.wireOp",EDGE,"E27.sketch_text.stroke-36")])],"isStart":true})});
            var Q19;
            Q19=makeQuery(id+"F12.boolean.opBoolean","COPY",EDGE,{"derivedFrom":makeQuery(id+"F12.opExtrude","CAP_EDGE",EDGE,{"disambiguationData":[OSD([sQuery(id+"F11.wireOp",EDGE,"E27.sketch_text.stroke-33")])],"isStart":true})});
            var Q20;
            Q20=makeQuery(id+"F12.boolean.opBoolean","COPY",EDGE,{"derivedFrom":makeQuery(id+"F12.opExtrude","CAP_EDGE",EDGE,{"disambiguationData":[OSD([sQuery(id+"F11.wireOp",EDGE,"E27.sketch_text.stroke-30")])],"isStart":true})});
            var Q21;
            Q21=makeQuery(id+"F12.boolean.opBoolean","COPY",EDGE,{"derivedFrom":makeQuery(id+"F12.opExtrude","CAP_EDGE",EDGE,{"disambiguationData":[OSD([sQuery(id+"F11.wireOp",EDGE,"E27.sketch_text.stroke-31")])],"isStart":true})});
            var Q22;
            Q22=makeQuery(id+"F12.boolean.opBoolean","COPY",EDGE,{"derivedFrom":makeQuery(id+"F12.opExtrude","CAP_EDGE",EDGE,{"disambiguationData":[OSD([sQuery(id+"F11.wireOp",EDGE,"E27.sketch_text.stroke-32")])],"isStart":true})});
            var Q23;
            Q23=makeQuery(id+"F12.boolean.opBoolean","COPY",EDGE,{"derivedFrom":makeQuery(id+"F12.opExtrude","CAP_EDGE",EDGE,{"disambiguationData":[OSD([sQuery(id+"F11.wireOp",EDGE,"E27.sketch_text.stroke-41")])],"isStart":true})});
            var Q24;
            Q24=makeQuery(id+"F12.boolean.opBoolean","COPY",EDGE,{"derivedFrom":makeQuery(id+"F12.opExtrude","CAP_EDGE",EDGE,{"disambiguationData":[OSD([sQuery(id+"F11.wireOp",EDGE,"E27.sketch_text.stroke-58")])],"isStart":true})});
            var Q25;
            Q25=makeQuery(id+"F12.boolean.opBoolean","COPY",EDGE,{"derivedFrom":makeQuery(id+"F12.opExtrude","CAP_EDGE",EDGE,{"disambiguationData":[OSD([sQuery(id+"F11.wireOp",EDGE,"E27.sketch_text.stroke-57")])],"isStart":true})});
            var Q26;
            Q26=makeQuery(id+"F12.boolean.opBoolean","COPY",EDGE,{"derivedFrom":makeQuery(id+"F12.opExtrude","CAP_EDGE",EDGE,{"disambiguationData":[OSD([sQuery(id+"F11.wireOp",EDGE,"E27.sketch_text.stroke-76")])],"isStart":true})});
            var Q27;
            Q27=makeQuery(id+"F12.boolean.opBoolean","COPY",EDGE,{"derivedFrom":makeQuery(id+"F12.opExtrude","CAP_EDGE",EDGE,{"disambiguationData":[OSD([sQuery(id+"F11.wireOp",EDGE,"E27.sketch_text.stroke-50")])],"isStart":true})});
            var Q28;
            Q28=makeQuery(id+"F12.boolean.opBoolean","COPY",EDGE,{"derivedFrom":makeQuery(id+"F12.opExtrude","CAP_EDGE",EDGE,{"disambiguationData":[OSD([sQuery(id+"F11.wireOp",EDGE,"E27.sketch_text.stroke-70")])],"isStart":true})});
            var Q29;
            Q29=makeQuery(id+"F12.boolean.opBoolean","COPY",EDGE,{"derivedFrom":makeQuery(id+"F12.opExtrude","CAP_EDGE",EDGE,{"disambiguationData":[OSD([sQuery(id+"F11.wireOp",EDGE,"E27.sketch_text.stroke-65")])],"isStart":true})});
            fillet(context, id + "F14", {"entities" : qUnion([Q0, Q1, Q2, Q3, Q4, Q5, Q6, Q7, Q8, Q9, Q10, Q11, Q12, Q13, Q14, Q15, Q16, Q17, Q18, Q19, Q20, Q21, Q22, Q23, Q24, Q25, Q26, Q27, Q28, Q29]), "radius" : .5 * mm, "tangentPropagation" : true, "allowEdgeOverflow" : false});
        }
    });
